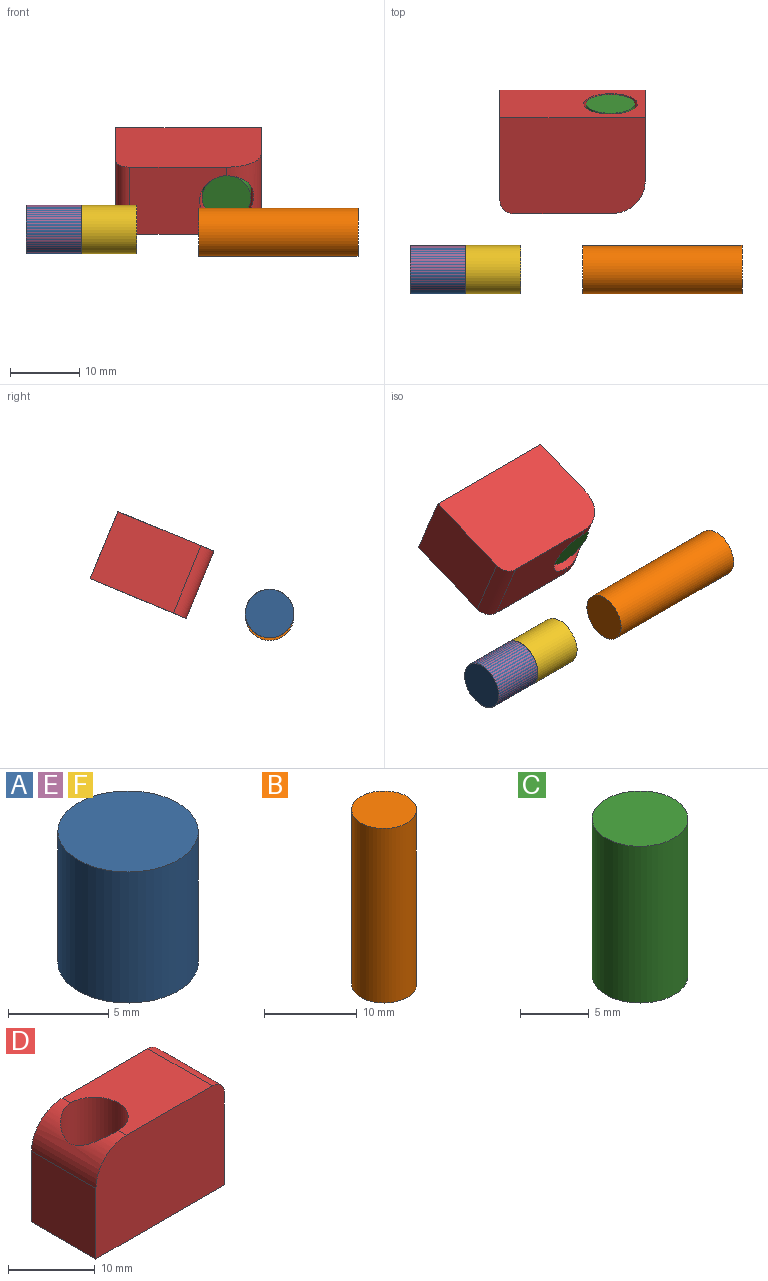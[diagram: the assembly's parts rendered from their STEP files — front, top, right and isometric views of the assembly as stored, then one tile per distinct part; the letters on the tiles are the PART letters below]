
ASSEMBLY  parts=6 mates=2
PART A: 3 faces, bbox 7x7x8 mm
  f0: cylinder r=3.5mm len=8mm, axis (0,0,-1), area 175.9mm2, adj f1,f2
  f1: plane 7x7mm, normal (0,0,1), area 38.5mm2, adj f0
  f2: plane 7x7mm, normal (0,0,-1), area 38.5mm2, adj f0
PART B: 3 faces, bbox 7x7x23 mm
  f0: cylinder r=3.5mm len=23mm, axis (0,0,-1), area 505.8mm2, adj f1,f2
  f1: plane 7x7mm, normal (0,0,1), area 38.5mm2, adj f0
  f2: plane 7x7mm, normal (0,0,-1), area 38.5mm2, adj f0
PART C: 3 faces, bbox 7x7x14 mm
  f0: cylinder r=3.5mm len=14mm, axis (0,0,-1), area 307.9mm2, adj f1,f2
  f1: plane 7x7mm, normal (0,0,1), area 38.5mm2, adj f0
  f2: plane 7x7mm, normal (0,0,-1), area 38.5mm2, adj f0
PART D: 9 faces, bbox 21x10.5x15 mm
  f0: plane 13x10.52mm, normal (1,0,0), area 136.7mm2, adj f1,f3,f6,f7
  f1: plane 21x15mm, normal (0,1,0), area 308.8mm2, adj f0,f2,f5,f6,f7,f8
  f2: plane 10.52x10mm, normal (-1,0,0), area 105.2mm2, adj f1,f3,f6,f8
  f3: plane 21x15mm, normal (0,-1,0), area 308.8mm2, adj f0,f2,f5,f6,f7,f8
  f4: cylinder r=3.9mm len=15mm, axis (0,0,-1), area 356.8mm2, adj f5,f6,f8
  f5: plane 14x10.52mm, normal (0,0,1), area 123.3mm2, adj f1,f3,f4,f7,f8
  f6: plane 21x10.52mm, normal (0,0,-1), area 173.1mm2, adj f0,f1,f2,f3,f4
  f7: cylinder r=2mm len=10.52mm, axis (0,-1,0), area 33mm2, adj f0,f1,f3,f5
  f8: cylinder r=5mm len=10.52mm, axis (0,1,0), area 56.3mm2, adj f1,f2,f3,f4,f5
PART E: same geometry as A
PART F: same geometry as A
PLACE A rot(axis=(0.58,0.58,0.58),120deg) t=(-75.91,-19.34,11.7)mm
PLACE B rot(axis=(0.58,-0.58,-0.58),120deg) t=(-27.91,-19.34,11.3)mm
PLACE C rot(axis=(0.64,0.64,-0.43),133.7deg) t=(-46.91,4.4,22.08)mm
PLACE D rot(axis=(0,-0.83,0.56),180deg) t=(-47.47,4.6,21.59)mm
PLACE E rot(axis=(-0.7,-0.14,0.7),164.2deg) t=(-67.91,-19.34,11.7)mm
PLACE F rot(axis=(0,-1,0),90deg) t=(-59.91,-19.34,11.7)mm
MATE revolute C.f0 <-> D.f4  axis (0,0.92,0.38) through (-46.91,4.6,21.59)mm
MATE fastened A.f0 <-> F.f0  axis (-1,0,0) through (-67.91,-19.34,11.7)mm
